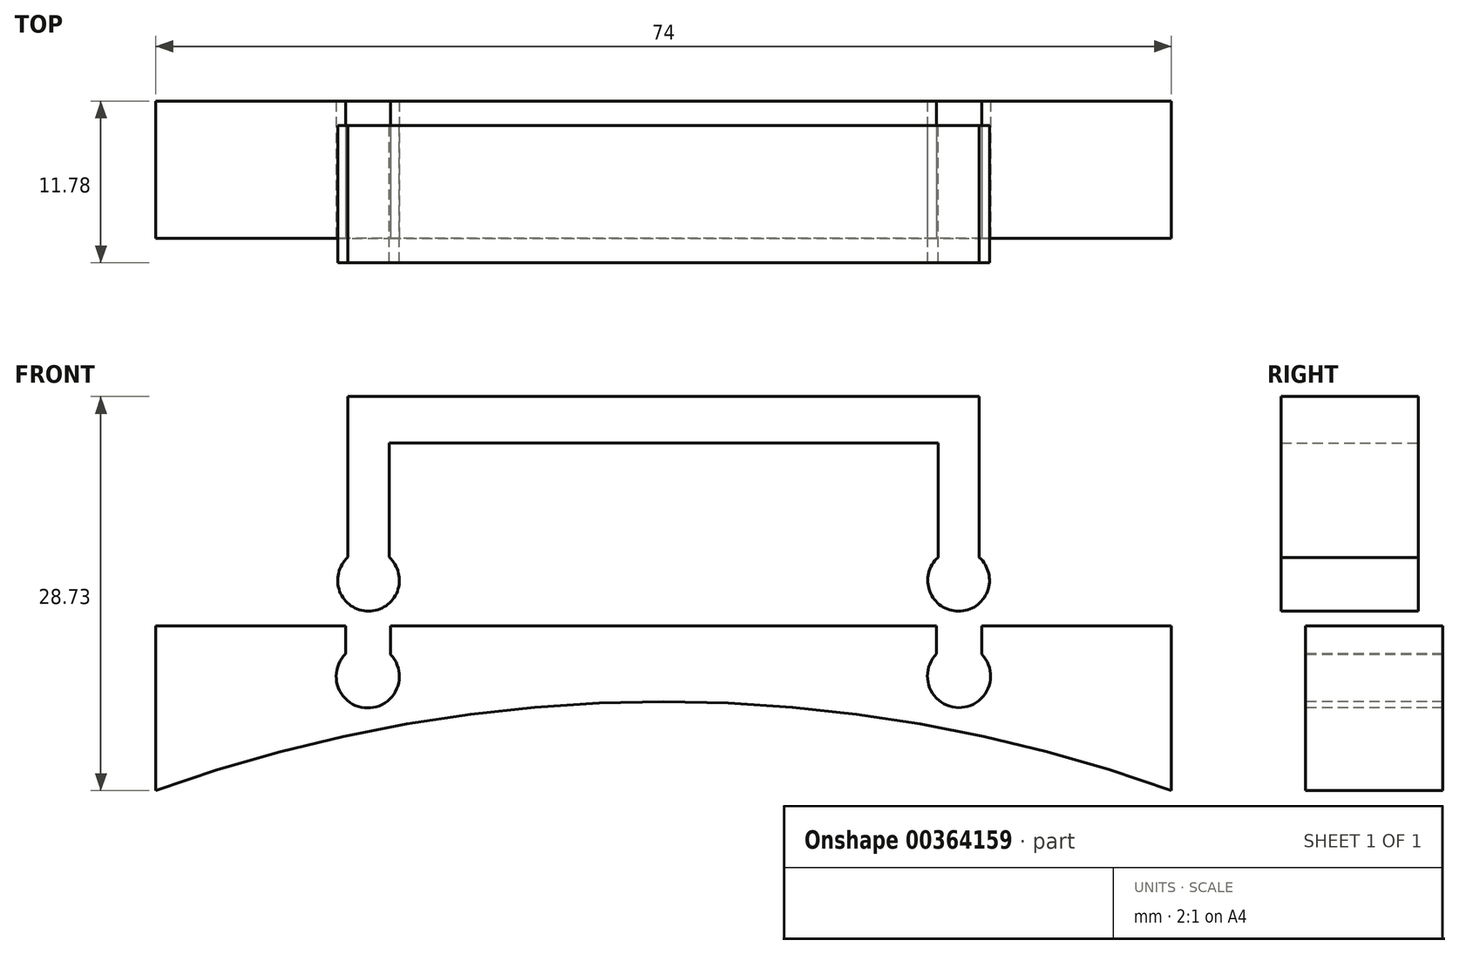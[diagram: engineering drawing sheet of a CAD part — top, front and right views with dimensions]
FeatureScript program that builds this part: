
annotation { "Feature Type Name" : "Feature", "Feature Type Description" : "" }
export const myFeature = defineFeature(function(context is Context, id is Id, definition is map)
    precondition{}
    {
        {
            var Q0;
            Q0=qCreatedBy(makeId("Top.planeOp"),FACE);
            var sketch = newSketch(context, id + "F0", { "sketchPlane" : qUnion([Q0])});
            skLineSegment(sketch, "E0.bottom", {"start": v(-38.95, 1.78) * mm, "end": v(35.05, 1.78) * mm});
            skLineSegment(sketch, "E0.top", {"start": v(-38.95, -8.22) * mm, "end": v(35.05, -8.22) * mm});
            skLineSegment(sketch, "E0.left", {"start": v(-38.95, 1.78) * mm, "end": v(-38.95, -8.22) * mm});
            skLineSegment(sketch, "E0.right", {"start": v(35.05, 1.78) * mm, "end": v(35.05, -8.22) * mm});
            skSolve(sketch);
        }
        {
            var Q0;
            Q0 = qSketchRegion(id + "F0", true);
            extrude(context, id + "F1", {"entities" : qUnion([Q0]), "depth" : 12 * mm});
        }
        {
            var Q0;
            Q0=makeQuery(id+"F1.opExtrude","SWEPT_FACE",FACE,{"disambiguationData":[OSD([sQuery(id+"F0.wireOp",EDGE,"E0.top")])]});
            var sketch = newSketch(context, id + "F2", { "sketchPlane" : qUnion([Q0])});
            skCircle(sketch, "E1", {"center": v(-1.95, -102.53) * mm, "radius": 109 * mm});
            skPoint(sketch, "E1.first.point", {"position": v(-38.95, 0) * mm});
            skPoint(sketch, "E1.second.point", {"position": v(35.05, 0) * mm});
            skPoint(sketch, "E1.third.point", {"position": v(94.3, -153.7) * mm});
            skSolve(sketch);
        }
        {
            var Q0;
            {var subQ1=sQuery(id+"F0.wireOp",EDGE,"E0.top");var subQ2=makeQuery(id+"F1.opExtrude","CAP_EDGE",EDGE,{"disambiguationData":[OSD([subQ1])],"isStart":true});Q0=makeQuery(id+"F2.imprint","IMPRINT",FACE,{"disambiguationData":[TD([[makeQuery(id+"F2.imprint","IMPRINT",EDGE,{"derivedFrom":subQ2}),1.0]])]});}
            extrude(context, id + "F3", {"entities" : qUnion([Q0]), "operationType" : NewBodyOperationType.REMOVE, "oppositeDirection" : true, "depth" : 10 * mm});
        }
        {
            var Q0;
            Q0=makeQuery(id+"F1.opExtrude","SWEPT_FACE",FACE,{"disambiguationData":[OSD([sQuery(id+"F0.wireOp",EDGE,"E0.top")])]});
            var sketch = newSketch(context, id + "F4", { "sketchPlane" : qUnion([Q0])});
            skSolve(sketch);
        }
        {
            var Q0;
            Q0=qCreatedBy(makeId("Front.planeOp"),FACE);
            var sketch = newSketch(context, id + "F5", { "sketchPlane" : qUnion([Q0])});
            skLineSegment(sketch, "E2", {"start": v(-21.95, 15.33) * mm, "end": v(-21.95, 25.33) * mm});
            skLineSegment(sketch, "E3", {"start": v(-21.95, 25.33) * mm, "end": v(18.05, 25.33) * mm});
            skLineSegment(sketch, "E4", {"start": v(18.05, 25.33) * mm, "end": v(18.05, 15.33) * mm});
            skLineSegment(sketch, "E5", {"start": v(21.05, 15.33) * mm, "end": v(21.05, 28.73) * mm});
            skLineSegment(sketch, "E6", {"start": v(-24.95, 15.33) * mm, "end": v(-24.95, 28.73) * mm});
            skLineSegment(sketch, "E7", {"start": v(-24.95, 28.73) * mm, "end": v(21.05, 28.73) * mm});
            skCircle(sketch, "E8", {"center": v(-23.45, 15.33) * mm, "radius": 2.25 * mm});
            skCircle(sketch, "E9", {"center": v(19.55, 15.33) * mm, "radius": 2.25 * mm});
            skSolve(sketch);
        }
        {
            var Q0;
            Q0 = qSketchRegion(id + "F5", true);
            extrude(context, id + "F6", {"entities" : qUnion([Q0]), "depth" : 10 * mm});
        }
        {
            var Q0;
            {var subQ0=sQuery(id+"F0.wireOp",EDGE,"E0.top");Q0=makeQuery(id+"F4.imprint","IMPRINT",FACE,{"disambiguationData":[TD([[makeQuery(id+"F4.imprint","IMPRINT",EDGE,{"derivedFrom":makeQuery(id+"F1.opExtrude","CAP_EDGE",EDGE,{"disambiguationData":[OSD([subQ0])],"isStart":false})}),-1.0]])]});}
            var sketch = newSketch(context, id + "F7", { "sketchPlane" : qUnion([Q0])});
            skLineSegment(sketch, "E10", {"start": v(21.24, 12) * mm, "end": v(17.95, 12) * mm});
            skLineSegment(sketch, "E11", {"start": v(-21.85, 12) * mm, "end": v(-25.1, 12) * mm});
            skLineSegment(sketch, "E12", {"start": v(21.24, 12) * mm, "end": v(21.24, 9.93) * mm});
            skLineSegment(sketch, "E13", {"start": v(17.95, 12) * mm, "end": v(17.95, 9.97) * mm});
            skLineSegment(sketch, "E14", {"start": v(-21.85, 12) * mm, "end": v(-21.85, 9.92) * mm});
            skLineSegment(sketch, "E15", {"start": v(-25.1, 12) * mm, "end": v(-25.1, 9.97) * mm});
            skCircle(sketch, "E16", {"center": v(19.58, 8.35) * mm, "radius": 2.3 * mm});
            skCircle(sketch, "E17", {"center": v(-23.5, 8.32) * mm, "radius": 2.3 * mm});
            skSolve(sketch);
        }
        {
            var Q0;
            Q0 = qSketchRegion(id + "F7", true);
            extrude(context, id + "F8", {"entities" : qUnion([Q0]), "operationType" : NewBodyOperationType.REMOVE, "oppositeDirection" : true, "depth" : 12 * mm});
        }
    });
